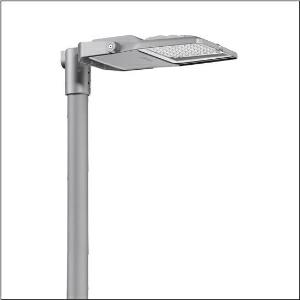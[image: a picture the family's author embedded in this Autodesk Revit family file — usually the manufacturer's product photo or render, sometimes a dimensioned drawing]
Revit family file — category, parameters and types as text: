
# Revit family: floodlight_fl_21_iq_mini___pl52_5xa7771c4d3a_e4a2
name_source: partatom
category: Lighting Fixtures
units: mm (PartAtom-declared; Revit-internal decimal feet)

## family parameters
Cut with Voids When Loaded = No
Host = Face
Light Source = No
Part Type = Normal
Room Calculation Point = No
Round Connector Dimension = Use Diameter
Shared = No

## types (1)
- --- (1 x LED, 12720 lm, 87.2 W, 4000K)
    Apparent Load = 87 VA
    CIE Flux Codes = 26 60 98 100 100
    Color Rendering = 70
    Color Temperature = 4000K
    Default Elevation = 1800 mm
    Description = Floodlight FL 21 iQ mini, floodlight, primary light control with lens, of PMMA, primary optical cover: protective disc, of toughened safety glass, transparent, light distribution: PL52, light emission: direct distribution, installation type: surface-mounted, LED, High Power LED, rated luminous flux: 12.720lm, luminous efficacy: 146lm/W, light colour: 740, colour temperature: 4000K, control: Auto-Match, Temp-Guard, Lumen-Switch, Night-Set, Smart-Wire, Light-Fading, Desk-Remote (wireless, voltage-free reading and setting of iQ features in the workshop via application-optimized NFC function/RFID function), optimised constant luminous flux control (CLO 2.0), with terminal, 6-pole, mains connection: 220..240V, AC, 50/60Hz, start of lifetime: 87W, end of service life: 92W, reduction: 40W, luminaire housing, of diecast aluminium, powder-coated, Siteco® metallic grey (DB 702S), corrosivity category C5 mid according to DIN EN ISO 12944, sealing non-destructively replaceable, please order mast flange separately, mast bracket, of steel, galvanised, powder-coated, Siteco® metallic grey (DB 702S), protection rating (complete): IP66, insulation class (complete): insulation class II (safety insulation), certification: CE, ENEC, VDE, protection symbol: D, impact resistance: IK08, permissible operating ambient temperature: -40..+40°C, permissible operating ambient temperature for outdoor applications: -40..+50°C, standard: DIN EN 12944, LABS conformity tested according to VDMA 24364:2018-05, packaging unit: 1 piece

Light Distribution: PL52
    Height = 70 mm
    Lamp = 1 x LED
    Lamp Light Flux = 12720 lm
    Lamp Power = 87.2 W
    Lamp count = 1
    Length = 485 mm
    Luminous efficacy = 146 lm/W
    Manufacturer = Siteco
    ModVariant = No
    Model = 5XA7771C4D3A
    Number of Poles = 1
    OnlyDefault = Yes
    Power Factor = 1
    Product Name = Floodlight FL 21 iQ mini | PL52
    Product group = floodlight | pylon annexe
    ProductGroupID = 6200
    Protection Class = Protection class II
    Protection Degree = IP 66
    RLX_Detail_Level = 1
    RLX_Emergency_Light_Flux = 0 lm
    RLX_Emergency_Type = 0
    RLX_Emergency_Type_DB = No
    RlxData = <blob elided: 101441 chars, md5=0230893f>
    Socket = socket
    Standby Power = 0 W
    System Light Flux = 12720 lm
    System Power = 87 W
    Type Comments = factory setting: luminous flux: 100 % | dim-lin: 254 | 456 mA
    Type Image = l_1007125.jpg
    URL = http://relux.com
    VarID = @adj_096747
    Voltage = 0 V
    Weight = 0.00 kg
    Width = 337 mm

## geometry (parser evidence)
native form markers: Blend x4, Sweep x13
no freeform markers — native parametric forms only
